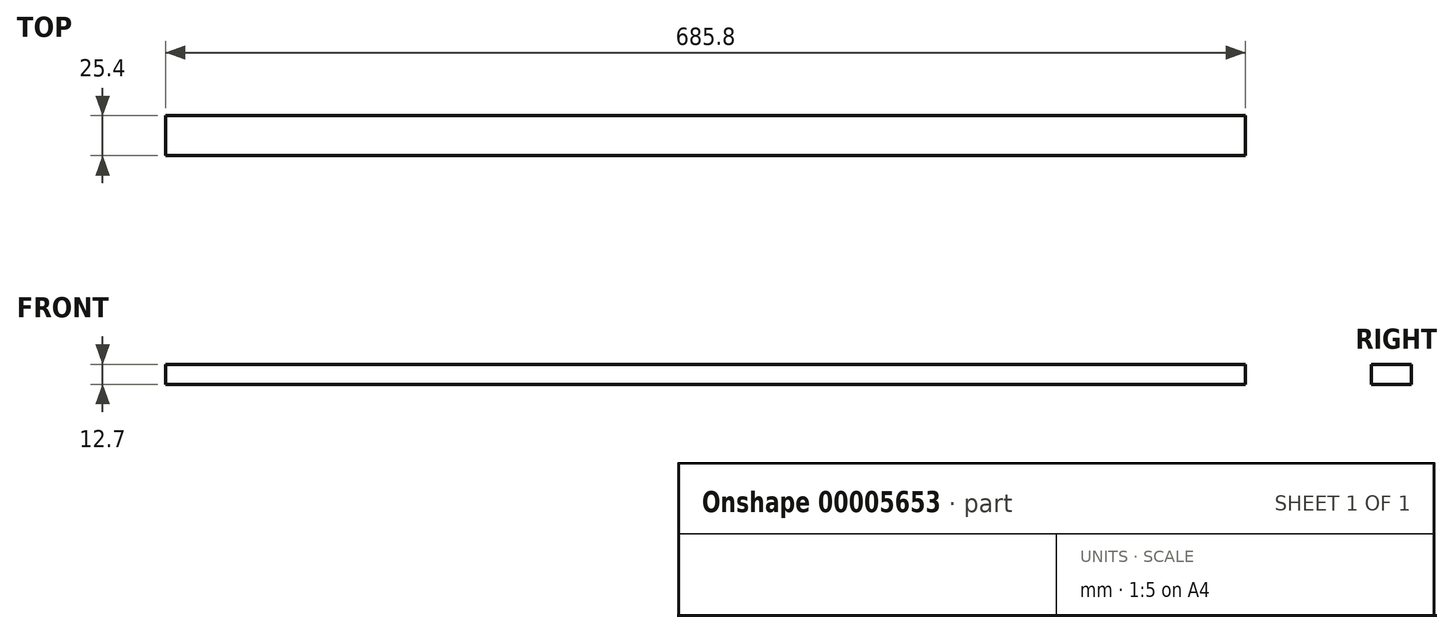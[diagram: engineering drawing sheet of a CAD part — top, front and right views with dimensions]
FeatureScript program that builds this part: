
annotation { "Feature Type Name" : "Feature", "Feature Type Description" : "" }
export const myFeature = defineFeature(function(context is Context, id is Id, definition is map)
    precondition{}
    {
        {
            var Q0;
            Q0=qCreatedBy(makeId("Top.planeOp"),FACE);
            var sketch = newSketch(context, id + "F0", { "sketchPlane" : qUnion([Q0])});
            skLineSegment(sketch, "E0.bottom", {"start": v(0, 0) * mm, "end": v(-685.8, 0) * mm});
            skLineSegment(sketch, "E0.top", {"start": v(0, -25.4) * mm, "end": v(-685.8, -25.4) * mm});
            skLineSegment(sketch, "E0.left", {"start": v(0, 0) * mm, "end": v(0, -25.4) * mm});
            skLineSegment(sketch, "E0.right", {"start": v(-685.8, 0) * mm, "end": v(-685.8, -25.4) * mm});
            skSolve(sketch);
        }
        {
            var Q0;
            Q0 = qSketchRegion(id + "F0", true);
            extrude(context, id + "F1", {"entities" : qUnion([Q0]), "depth" : 12.7 * mm});
        }
    });
